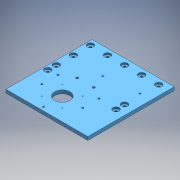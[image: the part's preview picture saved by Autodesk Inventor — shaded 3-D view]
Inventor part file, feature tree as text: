
AUTODESK INVENTOR PART (.ipt)
format: ipt  version: 2016 (Build 200138000, 138)  size: 200,704 bytes
history: native  units: mm
features: sketch x7, hole x5, extrude x2
ambient origin geometry x8: Origin, YZ Plane, XZ Plane, XY Plane, X Axis, Y Axis, Z Axis, Center Point
bodies: Solid1 (feature_tree)
feature tree (14):
  extrude  "baseExtrusion"  Depth=240.0mm
  extrude  "objectiveExtrusion"  Depth=252.5mm
  hole  "60mmCageRodThread"  [1 undecoded]
  hole  "m6BreadoardMountingHoles"  [1 undecoded]
  hole  "m4MirrorTLMountingHoles"  [1 undecoded]
  hole  "m6objectiveHolderMountingHoles"  [1 undecoded]
  hole  "filterwheelMountingHoles"  [1 undecoded]
  sketch  "Sketch1"  dims[d0=240.0mm d1=140.0mm]
  sketch  "Sketch2"  dims[d2=252.5mm d3=135.0mm]
  sketch  "Sketch3"  dims[d4=10.2mm d5=0.0mm d6=45.0mm]
  sketch  "Sketch4"  dims[d7=65.0mm d8=9.2mm d9=0.0mm]
  sketch  "Sketch5"  dims[d10=60.0mm d11=60.0mm]
  sketch  "Sketch6"  dims[d12=30.0mm]
  sketch  "Sketch7"  dims[d13=2.156mm d14=5.69mm d15=4.0mm d16=2.0mm d17=90.0deg d18=8.865mm d19=20.594885mm d20=200.0mm d21=100.0mm d23=70.0mm d24=6.6mm d25=5.69mm d26=18.0mm d27=4.8mm d28=90.0deg d29=8.865mm d30=20.594885mm d31=110.0mm d33=4.5mm d34=5.69mm d35=13.0mm d36=3.4mm d37=90.0deg d38=8.865mm d39=20.594885mm d40=8.4mm d41=30.0mm d42=120.0mm d43=60.0mm d44=47.5mm d45=55.0mm d46=30.0mm d47=4.917mm d48=12.0mm d49=4.0mm d50=2.0mm d51=90.0deg d52=17.1mm d53=20.594885mm d54=48.5mm d55=24.25mm d56=68.0mm d57=6.6mm d58=12.0mm d59=10.0mm d60=4.8mm d61=90.0deg d62=17.1mm d63=20.594885mm d72=98.9mm d73=10.2mm d74=100.0mm d75=25.0mm d76=50.0mm d77=50.0mm d78=12.5mm d79=50.0mm]
note: 5 required parameter values undecoded (feature->parameter linkage not recoverable at this tier; creation-order binding heuristic only, values carry confidence <= 0.55)
